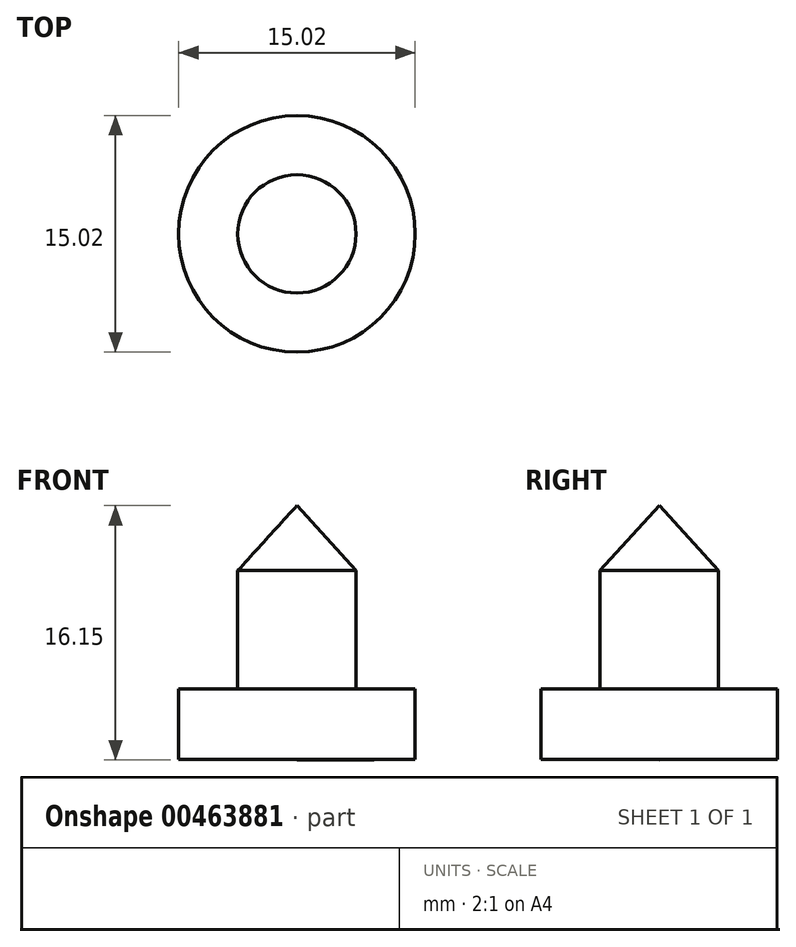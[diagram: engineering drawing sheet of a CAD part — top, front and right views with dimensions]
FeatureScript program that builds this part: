
annotation { "Feature Type Name" : "Feature", "Feature Type Description" : "" }
export const myFeature = defineFeature(function(context is Context, id is Id, definition is map)
    precondition{}
    {
        {
            var Q0;
            Q0=qCreatedBy(makeId("Front.planeOp"),FACE);
            var sketch = newSketch(context, id + "F0", { "sketchPlane" : qUnion([Q0])});
            skLineSegment(sketch, "E0", {"start": v(0, 11.64) * mm, "end": v(0, -4.5) * mm});
            skLineSegment(sketch, "E1", {"start": v(7.51, 0) * mm, "end": v(3.76, 0) * mm});
            skLineSegment(sketch, "E2", {"start": v(3.76, 0) * mm, "end": v(3.76, 7.51) * mm});
            skLineSegment(sketch, "E3", {"start": v(3.76, 7.51) * mm, "end": v(0, 11.64) * mm});
            skLineSegment(sketch, "E4", {"start": v(7.51, 0) * mm, "end": v(7.51, -4.49) * mm});
            skLineSegment(sketch, "E5", {"start": v(7.51, -4.49) * mm, "end": v(0, -4.5) * mm});
            skSolve(sketch);
        }
        {
            var Q0;
            Q0=makeQuery(id+"F0.imprint","IMPRINT",FACE,{"disambiguationData":[TD([[makeQuery(id+"F0.imprint","IMPRINT",EDGE,{"derivedFrom":sQuery(id+"F0.wireOp",EDGE,"E0")}),1.0]])]});
            var Q1;
            Q1=sQuery(id+"F0.wireOp",EDGE,"E0");
            revolve(context, id + "F1", {"entities" : qUnion([Q0]), "axis" : qUnion([Q1]), "revolveType" : RevolveType.FULL});
        }
    });
